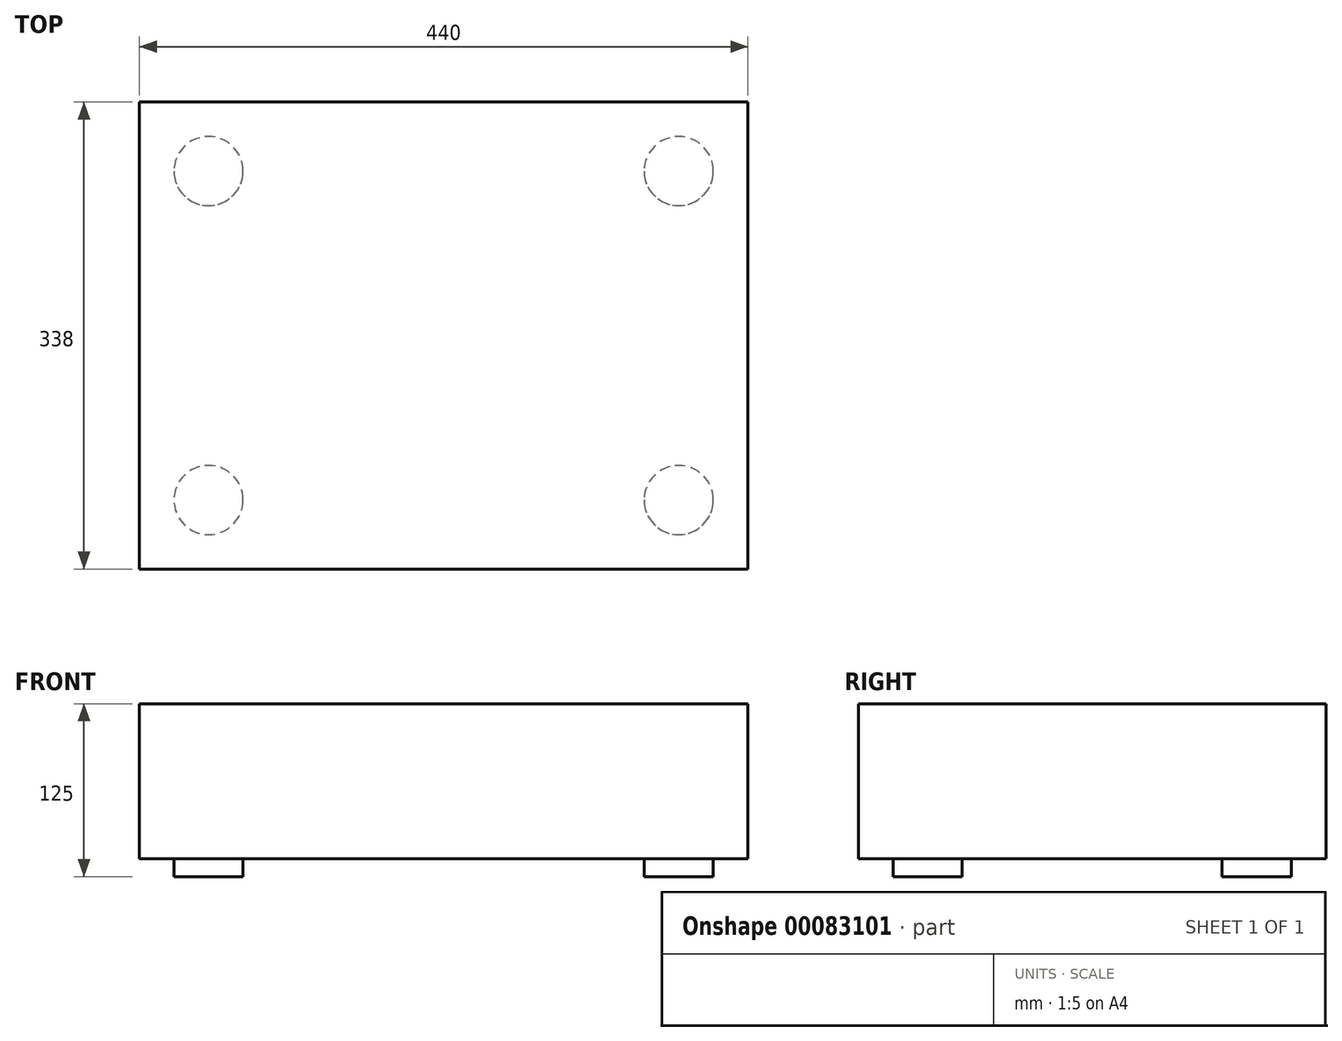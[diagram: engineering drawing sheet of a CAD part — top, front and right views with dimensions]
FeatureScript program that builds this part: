
annotation { "Feature Type Name" : "Feature", "Feature Type Description" : "" }
export const myFeature = defineFeature(function(context is Context, id is Id, definition is map)
    precondition{}
    {
        {
            var Q0;
            Q0=qCreatedBy(makeId("Top.planeOp"),FACE);
            var sketch = newSketch(context, id + "F0", { "sketchPlane" : qUnion([Q0])});
            skLineSegment(sketch, "E0.bottom", {"start": v(0, 0) * mm, "end": v(440, 0) * mm});
            skLineSegment(sketch, "E0.top", {"start": v(0, 338) * mm, "end": v(440, 338) * mm});
            skLineSegment(sketch, "E0.left", {"start": v(0, 0) * mm, "end": v(0, 338) * mm});
            skLineSegment(sketch, "E0.right", {"start": v(440, 0) * mm, "end": v(440, 338) * mm});
            skSolve(sketch);
        }
        {
            var Q0;
            Q0=qSketchRegion(id+"F0",true);
            extrude(context, id + "F1", {"entities" : qUnion([Q0]), "depth" : (125 - 13) * mm});
        }
        {
            var Q0;
            Q0=makeQuery(id+"F1.opExtrude","CAP_FACE",FACE,{"disambiguationData":[OSD([sQuery(id+"F0.wireOp",EDGE,"E0.bottom"),sQuery(id+"F0.wireOp",EDGE,"E0.top"),sQuery(id+"F0.wireOp",EDGE,"E0.left"),sQuery(id+"F0.wireOp",EDGE,"E0.right")])],"isStart":true});
            var sketch = newSketch(context, id + "F2", { "sketchPlane" : qUnion([Q0])});
            skCircle(sketch, "E1", {"center": v(50, -50) * mm, "radius": 25 * mm});
            skCircle(sketch, "E2.0.1.0", {"center": v(50, -288) * mm, "radius": 25 * mm});
            skCircle(sketch, "E2.1.0.0", {"center": v(390, -50) * mm, "radius": 25 * mm});
            skCircle(sketch, "E2.1.1.0", {"center": v(390, -288) * mm, "radius": 25 * mm});
            skLineSegment(sketch, "E2.direction1", {"start": v(50, -50) * mm, "end": v(390, -50) * mm, "construction": true});
            skLineSegment(sketch, "E2.direction2", {"start": v(50, -50) * mm, "end": v(50, -288) * mm, "construction": true});
            skSolve(sketch);
        }
        {
            var Q0;
            Q0=makeQuery(id+"F2.imprint","IMPRINT",FACE,{"disambiguationData":[TD([[makeQuery(id+"F2.imprint","IMPRINT",EDGE,{"derivedFrom":sQuery(id+"F2.wireOp",EDGE,"E1")}),1.0]])]});
            var Q1;
            Q1=makeQuery(id+"F2.imprint","IMPRINT",FACE,{"disambiguationData":[TD([[makeQuery(id+"F2.imprint","IMPRINT",EDGE,{"derivedFrom":sQuery(id+"F2.wireOp",EDGE,"E2.1.0.0")}),1.0]])]});
            var Q2;
            Q2=makeQuery(id+"F2.imprint","IMPRINT",FACE,{"disambiguationData":[TD([[makeQuery(id+"F2.imprint","IMPRINT",EDGE,{"derivedFrom":sQuery(id+"F2.wireOp",EDGE,"E2.1.1.0")}),1.0]])]});
            var Q3;
            Q3=makeQuery(id+"F2.imprint","IMPRINT",FACE,{"disambiguationData":[TD([[makeQuery(id+"F2.imprint","IMPRINT",EDGE,{"derivedFrom":sQuery(id+"F2.wireOp",EDGE,"E2.0.1.0")}),1.0]])]});
            extrude(context, id + "F3", {"entities" : qUnion([Q0, Q1, Q2, Q3]), "operationType" : NewBodyOperationType.ADD, "depth" : 13 * mm});
        }
    });
